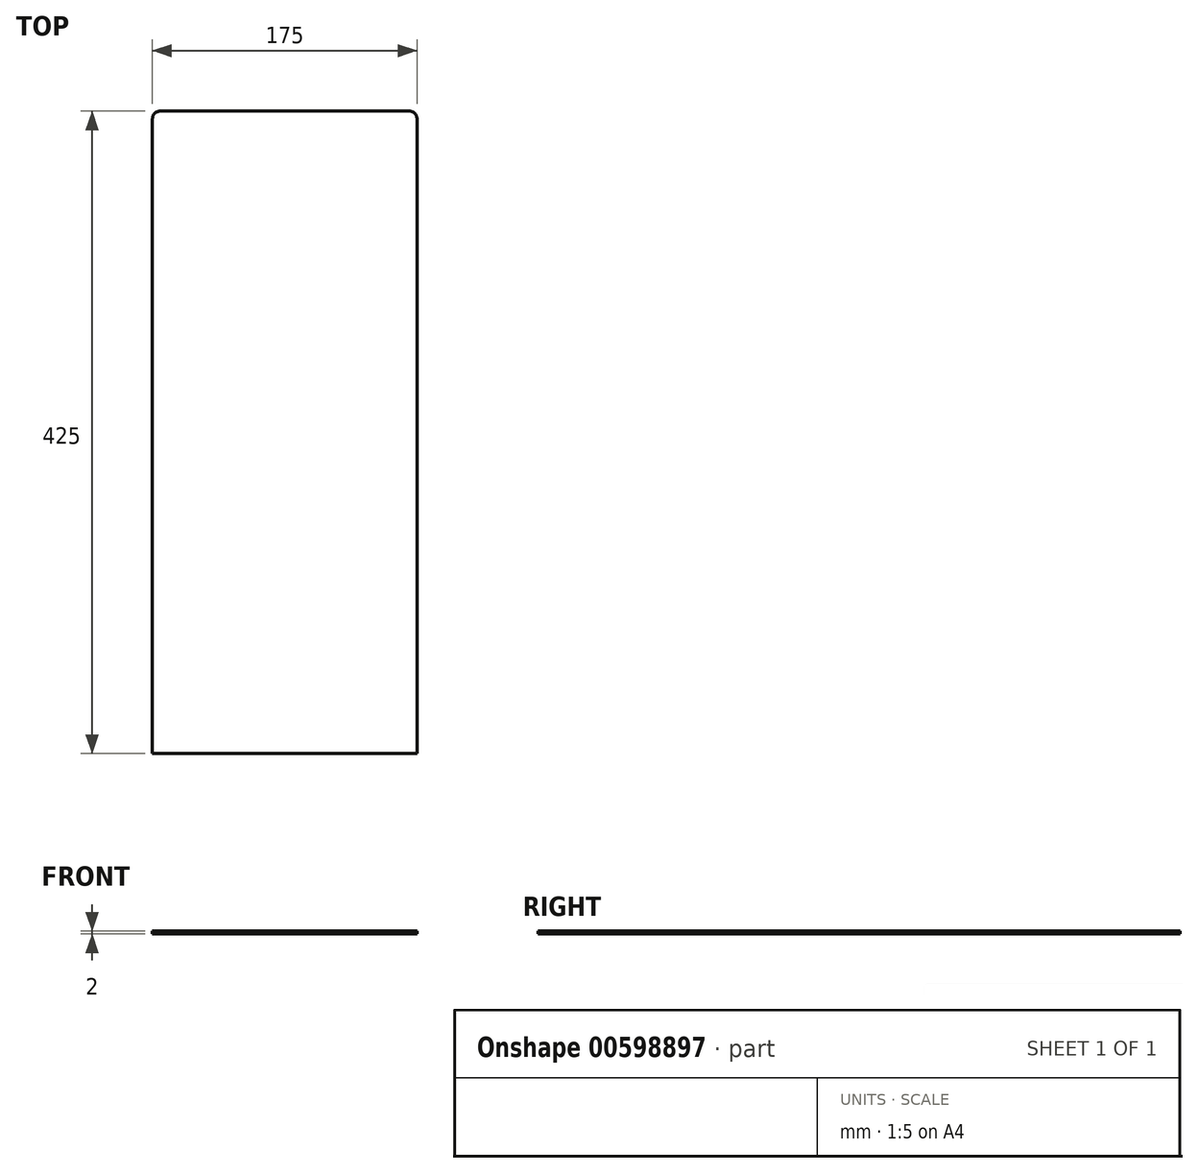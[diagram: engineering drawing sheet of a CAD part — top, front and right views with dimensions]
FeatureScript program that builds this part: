
annotation { "Feature Type Name" : "Feature", "Feature Type Description" : "" }
export const myFeature = defineFeature(function(context is Context, id is Id, definition is map)
    precondition{}
    {
        {
            var Q0;
            Q0=qCreatedBy(makeId("Top.planeOp"),FACE);
            var sketch = newSketch(context, id + "F0", { "sketchPlane" : qUnion([Q0])});
            skLineSegment(sketch, "E0.bottom", {"start": v(87.5, -202.5) * mm, "end": v(-87.5, -202.5) * mm});
            skLineSegment(sketch, "E0.top", {"start": v(87.5, 202.5) * mm, "end": v(-87.5, 202.5) * mm});
            skLineSegment(sketch, "E0.left", {"start": v(87.5, -202.5) * mm, "end": v(87.5, 202.5) * mm});
            skLineSegment(sketch, "E0.right", {"start": v(-87.5, -202.5) * mm, "end": v(-87.5, 202.5) * mm});
            skPoint(sketch, "E0.middle", {"position": v(0, 0) * mm});
            skLineSegment(sketch, "E1", {"start": v(-87.5, 202.5) * mm, "end": v(-87.5, 222.5) * mm});
            skLineSegment(sketch, "E2", {"start": v(-87.5, 222.5) * mm, "end": v(87.5, 222.5) * mm});
            skLineSegment(sketch, "E3", {"start": v(87.5, 222.5) * mm, "end": v(87.5, 202.5) * mm});
            skSolve(sketch);
        }
        {
            var Q0;
            Q0=qSketchRegion(id+"F0",true);
            extrude(context, id + "F1", {"entities" : qUnion([Q0]), "depth" : 2 * mm, "offsetDistance" : 25 * mm});
        }
        {
            var Q0;
            Q0=makeQuery(id+"F1.opExtrude","SWEPT_EDGE",EDGE,{"disambiguationData":[OSD([sQuery(id+"F0.wireOp",EDGE,"E2"),sQuery(id+"F0.wireOp",EDGE,"E3")])]});
            var Q1;
            Q1=makeQuery(id+"F1.opExtrude","SWEPT_EDGE",EDGE,{"disambiguationData":[OSD([sQuery(id+"F0.wireOp",EDGE,"E1"),sQuery(id+"F0.wireOp",EDGE,"E2")])]});
            fillet(context, id + "F2", {"entities" : qUnion([Q0, Q1]), "radius" : 5 * mm, "tangentPropagation" : true, "allowEdgeOverflow" : false});
        }
    });
